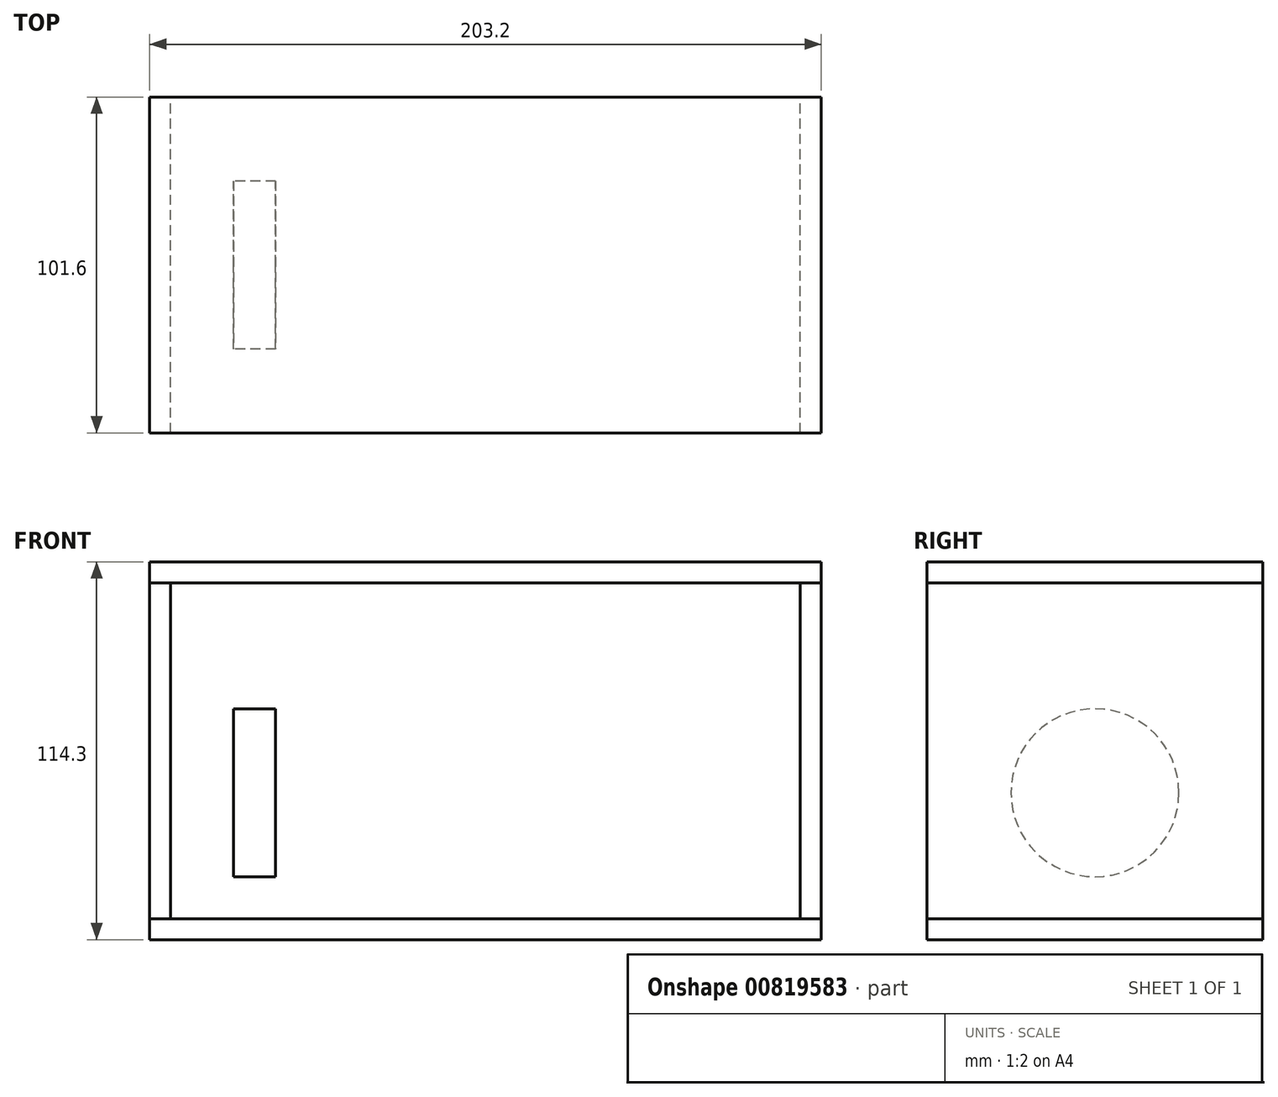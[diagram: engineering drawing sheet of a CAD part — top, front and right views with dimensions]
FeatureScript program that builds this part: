
annotation { "Feature Type Name" : "Feature", "Feature Type Description" : "" }
export const myFeature = defineFeature(function(context is Context, id is Id, definition is map)
    precondition{}
    {
        {
            assignVariable(context, id + "F0", {"name" : "depth", "anyValue" : 101.6 * mm});
        }
        {
            var Q0;
            Q0=qCreatedBy(makeId("Front.planeOp"),FACE);
            var sketch = newSketch(context, id + "F1", { "sketchPlane" : qUnion([Q0])});
            skLineSegment(sketch, "E0", {"start": v(-101.6, 0) * mm, "end": v(101.6, 0) * mm});
            skLineSegment(sketch, "E1", {"start": v(-101.6, 0) * mm, "end": v(-101.6, 114.3) * mm});
            skLineSegment(sketch, "E2", {"start": v(-101.6, 114.3) * mm, "end": v(101.6, 114.3) * mm});
            skLineSegment(sketch, "E3", {"start": v(101.6, 114.3) * mm, "end": v(101.6, 0) * mm});
            skLineSegment(sketch, "E4", {"start": v(-101.6, 107.95) * mm, "end": v(101.6, 107.95) * mm});
            skLineSegment(sketch, "E5", {"start": v(-101.6, 6.35) * mm, "end": v(101.6, 6.35) * mm});
            skLineSegment(sketch, "E6", {"start": v(-95.25, 107.95) * mm, "end": v(-95.25, 6.35) * mm});
            skLineSegment(sketch, "E7", {"start": v(95.25, 107.95) * mm, "end": v(95.25, 6.35) * mm});
            skLineSegment(sketch, "E8", {"start": v(0, 114.3) * mm, "end": v(0, 107.95) * mm, "construction": true});
            skLineSegment(sketch, "E9", {"start": v(-101.6, 57.15) * mm, "end": v(-95.25, 57.15) * mm, "construction": true});
            skLineSegment(sketch, "E10", {"start": v(0, 6.35) * mm, "end": v(0, 0) * mm, "construction": true});
            skLineSegment(sketch, "E11", {"start": v(95.25, 57.15) * mm, "end": v(101.6, 57.15) * mm, "construction": true});
            skLineSegment(sketch, "E12", {"start": v(-95.25, 57.15) * mm, "end": v(95.25, 57.15) * mm});
            skLineSegment(sketch, "E13.bottom", {"start": v(-76.2, 69.85) * mm, "end": v(-63.5, 69.85) * mm});
            skLineSegment(sketch, "E13.top", {"start": v(-76.2, 19.05) * mm, "end": v(-63.5, 19.05) * mm});
            skLineSegment(sketch, "E13.left", {"start": v(-76.2, 69.85) * mm, "end": v(-76.2, 19.05) * mm});
            skLineSegment(sketch, "E13.right", {"start": v(-63.5, 69.85) * mm, "end": v(-63.5, 19.05) * mm});
            skLineSegment(sketch, "E14.bottom", {"start": v(-6.35, 88.9) * mm, "end": v(6.35, 88.9) * mm});
            skLineSegment(sketch, "E14.top", {"start": v(-6.35, 38.1) * mm, "end": v(6.35, 38.1) * mm});
            skLineSegment(sketch, "E14.left", {"start": v(-6.35, 88.9) * mm, "end": v(-6.35, 38.1) * mm});
            skLineSegment(sketch, "E14.right", {"start": v(6.35, 88.9) * mm, "end": v(6.35, 38.1) * mm});
            skLineSegment(sketch, "E15.bottom", {"start": v(63.5, 88.9) * mm, "end": v(76.2, 88.9) * mm});
            skLineSegment(sketch, "E15.top", {"start": v(63.5, 38.1) * mm, "end": v(76.2, 38.1) * mm});
            skLineSegment(sketch, "E15.left", {"start": v(63.5, 88.9) * mm, "end": v(63.5, 38.1) * mm});
            skLineSegment(sketch, "E15.right", {"start": v(76.2, 88.9) * mm, "end": v(76.2, 38.1) * mm});
            skLineSegment(sketch, "E16", {"start": v(-76.2, 44.45) * mm, "end": v(-63.5, 44.45) * mm});
            skLineSegment(sketch, "E17", {"start": v(-69.85, 57.15) * mm, "end": v(-69.85, 44.45) * mm, "construction": true});
            skLineSegment(sketch, "E18", {"start": v(-6.35, 63.5) * mm, "end": v(6.35, 63.5) * mm});
            skLineSegment(sketch, "E19", {"start": v(63.5, 63.5) * mm, "end": v(76.2, 63.5) * mm});
            skLineSegment(sketch, "E20", {"start": v(0, 57.15) * mm, "end": v(0, 63.5) * mm, "construction": true});
            skLineSegment(sketch, "E21", {"start": v(69.85, 63.5) * mm, "end": v(69.85, 57.15) * mm, "construction": true});
            skSolve(sketch);
        }
        {
            var Q0;
            {var subQ1=sQuery(id+"F1.wireOp",EDGE,"E2");Q0=makeQuery(id+"F1.imprint","IMPRINT",FACE,{"disambiguationData":[TD([[makeQuery(id+"F1.imprint","IMPRINT",EDGE,{"derivedFrom":subQ1}),-1.0]])]});}
            var Q1;
            {var subQ1=sQuery(id+"F1.wireOp",EDGE,"E0");Q1=makeQuery(id+"F1.imprint","IMPRINT",FACE,{"disambiguationData":[TD([[makeQuery(id+"F1.imprint","IMPRINT",EDGE,{"derivedFrom":subQ1}),1.0]])]});}
            extrude(context, id + "F2", {"entities" : qUnion([Q0, Q1]), "endBound" : BoundingType.SYMMETRIC, "depth" : getVariable(context, 'depth'), "offsetDistance" : 25.4 * mm});
        }
        {
            var Q0;
            {var subQ5=sQuery(id+"F1.wireOp",EDGE,"E6");Q0=makeQuery(id+"F1.imprint","IMPRINT",FACE,{"disambiguationData":[TD([[makeQuery(id+"F1.imprint","IMPRINT",EDGE,{"derivedFrom":subQ5}),-1.0]])]});}
            var Q1;
            {var subQ5=sQuery(id+"F1.wireOp",EDGE,"E7");Q1=makeQuery(id+"F1.imprint","IMPRINT",FACE,{"disambiguationData":[TD([[makeQuery(id+"F1.imprint","IMPRINT",EDGE,{"derivedFrom":subQ5}),1.0]])]});}
            var Q2;
            Q2=makeQuery(id+"F2.opExtrude","CAP_FACE",FACE,{"disambiguationData":[OSD([sQuery(id+"F1.wireOp",EDGE,"E1"),sQuery(id+"F1.wireOp",EDGE,"E2"),sQuery(id+"F1.wireOp",EDGE,"E3"),sQuery(id+"F1.wireOp",EDGE,"E4")])],"isStart":false});
            var Q3;
            Q3=makeQuery(id+"F2.opExtrude","CAP_FACE",FACE,{"disambiguationData":[OSD([sQuery(id+"F1.wireOp",EDGE,"E1"),sQuery(id+"F1.wireOp",EDGE,"E2"),sQuery(id+"F1.wireOp",EDGE,"E3"),sQuery(id+"F1.wireOp",EDGE,"E4")])],"isStart":true});
            extrude(context, id + "F3", {"entities" : qUnion([Q0, Q1]), "endBound" : BoundingType.UP_TO_SURFACE, "depth" : 101.6 * mm, "endBoundEntityFace" : qUnion([Q2]), "offsetDistance" : 25.4 * mm, "hasSecondDirection" : true, "secondDirectionBound" : SecondDirectionBoundingType.UP_TO_SURFACE, "secondDirectionOppositeDirection" : true, "secondDirectionDepth" : 25.4 * mm, "secondDirectionBoundEntityFace" : qUnion([Q3])});
        }
        {
            var Q0;
            {var subQ0=sQuery(id+"F1.wireOp",EDGE,"E13.top");Q0=makeQuery(id+"F1.imprint","IMPRINT",FACE,{"disambiguationData":[TD([[makeQuery(id+"F1.imprint","IMPRINT",EDGE,{"derivedFrom":subQ0}),1.0]])]});}
            var Q1;
            Q1=sQuery(id+"F1.wireOp",EDGE,"E16");
            revolve(context, id + "F4", {"surfaceOperationType" : NewSurfaceOperationType.NEW, "entities" : qUnion([Q0]), "axis" : qUnion([Q1]), "revolveType" : RevolveType.FULL});
        }
    });
